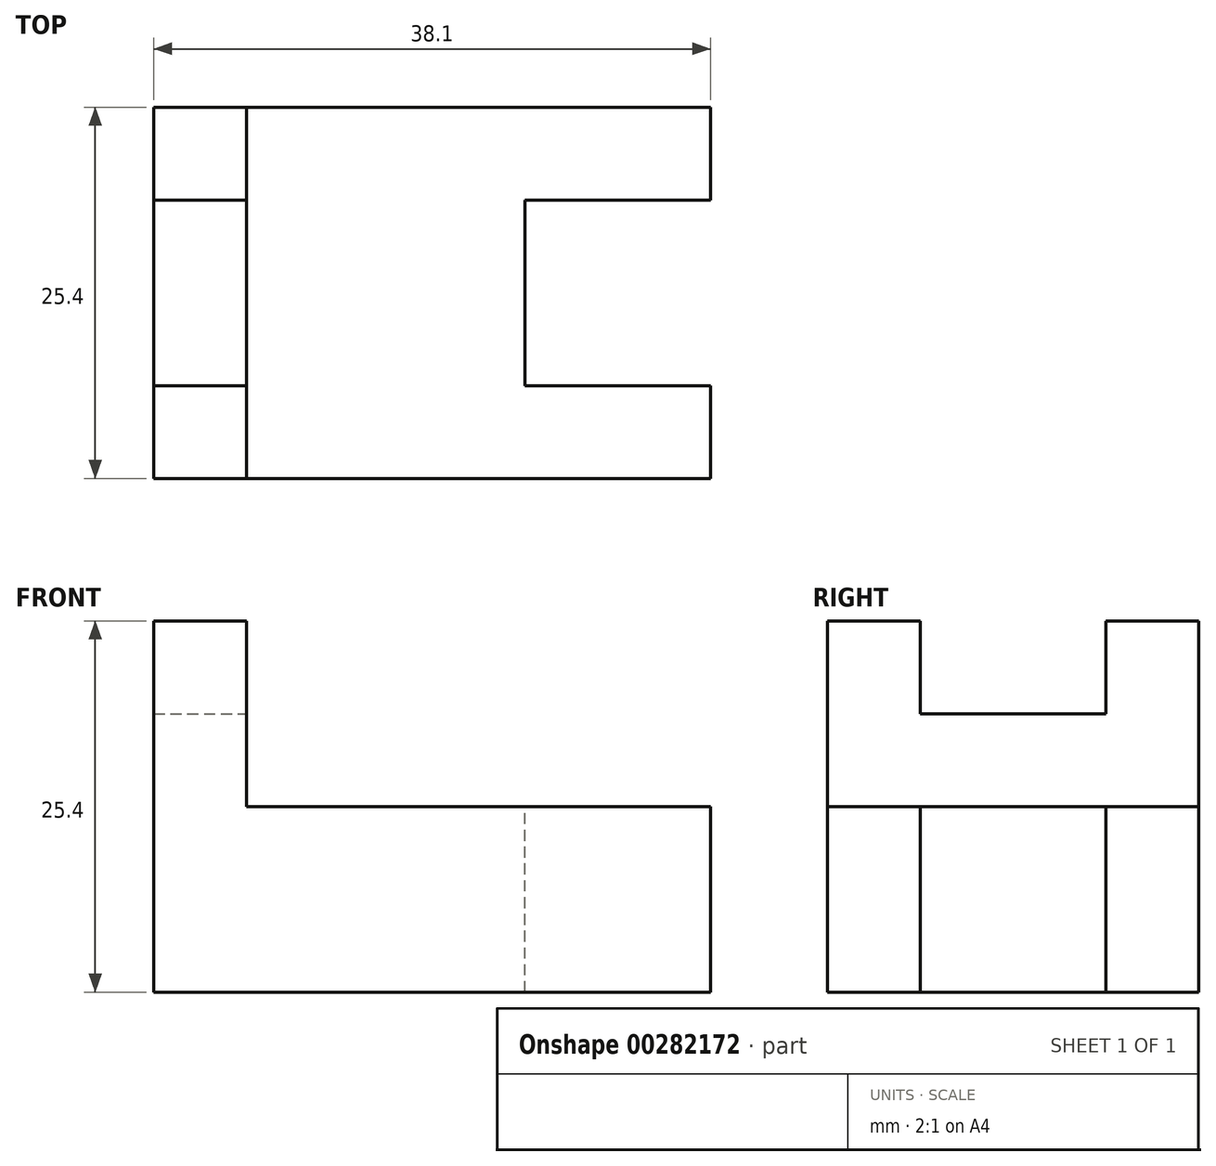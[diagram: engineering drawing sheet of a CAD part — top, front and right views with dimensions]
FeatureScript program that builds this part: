
annotation { "Feature Type Name" : "Feature", "Feature Type Description" : "" }
export const myFeature = defineFeature(function(context is Context, id is Id, definition is map)
    precondition{}
    {
        {
            var Q0;
            Q0=qCreatedBy(makeId("Front.planeOp"),FACE);
            var sketch = newSketch(context, id + "F0", { "sketchPlane" : qUnion([Q0])});
            skLineSegment(sketch, "E0", {"start": v(0, 0) * mm, "end": v(0, 25.4) * mm});
            skLineSegment(sketch, "E1", {"start": v(0, 25.4) * mm, "end": v(6.35, 25.4) * mm});
            skLineSegment(sketch, "E2", {"start": v(6.35, 25.4) * mm, "end": v(6.35, 12.7) * mm});
            skLineSegment(sketch, "E3", {"start": v(6.35, 12.7) * mm, "end": v(38.1, 12.7) * mm});
            skLineSegment(sketch, "E4", {"start": v(38.1, 12.7) * mm, "end": v(38.1, 0) * mm});
            skLineSegment(sketch, "E5", {"start": v(38.1, 0) * mm, "end": v(0, 0) * mm});
            skSolve(sketch);
        }
        {
            var Q0;
            Q0=makeQuery(id+"F0.imprint","IMPRINT",FACE,{"disambiguationData":[TD([[makeQuery(id+"F0.imprint","IMPRINT",EDGE,{"derivedFrom":sQuery(id+"F0.wireOp",EDGE,"E0")}),-1.0]])]});
            extrude(context, id + "F1", {"entities" : qUnion([Q0]), "depth" : 25.4 * mm, "symmetric" : true});
        }
        {
            var Q0;
            Q0=makeQuery(id+"F1.opExtrude","SWEPT_FACE",FACE,{"disambiguationData":[OSD([sQuery(id+"F0.wireOp",EDGE,"E1")])]});
            var sketch = newSketch(context, id + "F2", { "sketchPlane" : qUnion([Q0])});
            skLineSegment(sketch, "E6", {"start": v(0, 6.35) * mm, "end": v(6.35, 6.35) * mm});
            skLineSegment(sketch, "E7", {"start": v(6.35, 6.35) * mm, "end": v(6.35, -6.35) * mm});
            skLineSegment(sketch, "E8", {"start": v(6.35, -6.35) * mm, "end": v(0, -6.35) * mm});
            skLineSegment(sketch, "E9", {"start": v(0, -6.35) * mm, "end": v(0, 6.35) * mm});
            skSolve(sketch);
        }
        {
            var Q0;
            Q0=makeQuery(id+"F2.imprint","IMPRINT",FACE,{"disambiguationData":[TD([[makeQuery(id+"F2.imprint","IMPRINT",EDGE,{"derivedFrom":sQuery(id+"F2.wireOp",EDGE,"E6")}),-1.0]])]});
            extrude(context, id + "F3", {"entities" : qUnion([Q0]), "operationType" : NewBodyOperationType.REMOVE, "oppositeDirection" : true, "depth" : 6.35 * mm});
        }
        {
            var Q0;
            Q0=makeQuery(id+"F1.opExtrude","SWEPT_FACE",FACE,{"disambiguationData":[OSD([sQuery(id+"F0.wireOp",EDGE,"E3")])]});
            var sketch = newSketch(context, id + "F4", { "sketchPlane" : qUnion([Q0])});
            skLineSegment(sketch, "E10", {"start": v(38.1, 6.35) * mm, "end": v(25.4, 6.35) * mm});
            skLineSegment(sketch, "E11", {"start": v(25.4, 6.35) * mm, "end": v(25.4, -6.35) * mm});
            skLineSegment(sketch, "E12", {"start": v(25.4, -6.35) * mm, "end": v(38.1, -6.35) * mm});
            skSolve(sketch);
        }
        {
            var Q0;
            {var subQ0=sQuery(id+"F4.wireOp",EDGE,"E10");Q0=makeQuery(id+"F4.imprint","IMPRINT",FACE,{"disambiguationData":[TD([[makeQuery(id+"F4.imprint","IMPRINT",EDGE,{"derivedFrom":subQ0}),1.0]])]});}
            extrude(context, id + "F5", {"entities" : qUnion([Q0]), "operationType" : NewBodyOperationType.REMOVE, "oppositeDirection" : true, "depth" : 25.4 * mm});
        }
    });
